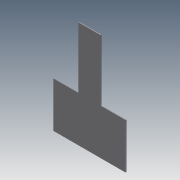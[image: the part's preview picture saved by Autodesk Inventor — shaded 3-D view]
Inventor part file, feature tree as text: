
AUTODESK INVENTOR PART (.ipt)
format: ipt  version: 2011 (Build 150239000, 239)  size: 180,736 bytes
history: native  units: in
note: dims shown in document units (in); Inventor stores cm internally (conversion verified against a paired STEP export)
features: extrude x14, sketch x14
ambient origin geometry x8: Origin, YZ Plane, XZ Plane, XY Plane, X Axis, Y Axis, Z Axis, Center Point
bodies: Solid1 (feature_tree)
feature tree (28):
  extrude  "Extrusion1"  Depth=35.0in
  extrude  "Extrusion2"  Depth=7.0in
  extrude  "Extrusion3"  Depth=7.0in
  extrude  "Extrusion4"  Depth=1.0in TaperAngle=0.0deg
  extrude  "Extrusion5"  Depth=0.25in TaperAngle=0.0deg
  extrude  "Extrusion6"  Depth=19.638in
  extrude  "Extrusion7"  Depth=1.0in TaperAngle=0.0deg
  extrude  "Extrusion8"  Depth=0.185in
  extrude  "Extrusion9"  Depth=15.0in
  extrude  "Extrusion10"  Depth=1.0in TaperAngle=0.0deg
  extrude  "Extrusion11"  Depth=12.5in
  extrude  "Extrusion12"  Depth=0.25in TaperAngle=0.0deg
  extrude  "Extrusion13"  Depth=3.86in
  extrude  "Extrusion14"  Depth=0.25in TaperAngle=0.0deg
  sketch  "Sketch1"  dims[d0=20.248in d1=35.0in]
  sketch  "Sketch3"  dims[d2=0.25in d3=0.0in d4=7.0in]
  sketch  "Sketch4"  dims[d5=18.14in d6=7.0in]
  sketch  "Sketch5"  dims[d7=18.14in d8=1.0in d9=0.0in]
  sketch  "Sketch6"  dims[d10=0.25in d11=0.0in d12=0.25in d13=0.0in]
  sketch  "Sketch7"  dims[d14=0.25in d15=0.0in d16=19.638in]
  sketch  "Sketch8"  dims[d17=0.185in d18=1.0in d19=0.0in]
  sketch  "Sketch9"  dims[d20=9.075in d21=0.185in]
  sketch  "Sketch10"  dims[d22=1.0in d23=0.0in d24=15.0in]
  sketch  "Sketch11"  dims[d25=0.612in d26=1.0in d27=0.0in]
  sketch  "Sketch12"  dims[d28=0.25in d29=0.0in d30=12.5in]
  sketch  "Sketch13"  dims[d31=0.25in d32=0.25in d33=0.0in]
  sketch  "Sketch14"  dims[d34=3.86in d35=3.86in]
  sketch  "Sketch15"  dims[d36=0.25in d37=0.0in d38=0.25in d39=0.0in d40=0.75in d41=1.0in d42=0.0in d43=0.5in d44=1.0in d45=0.0in]
